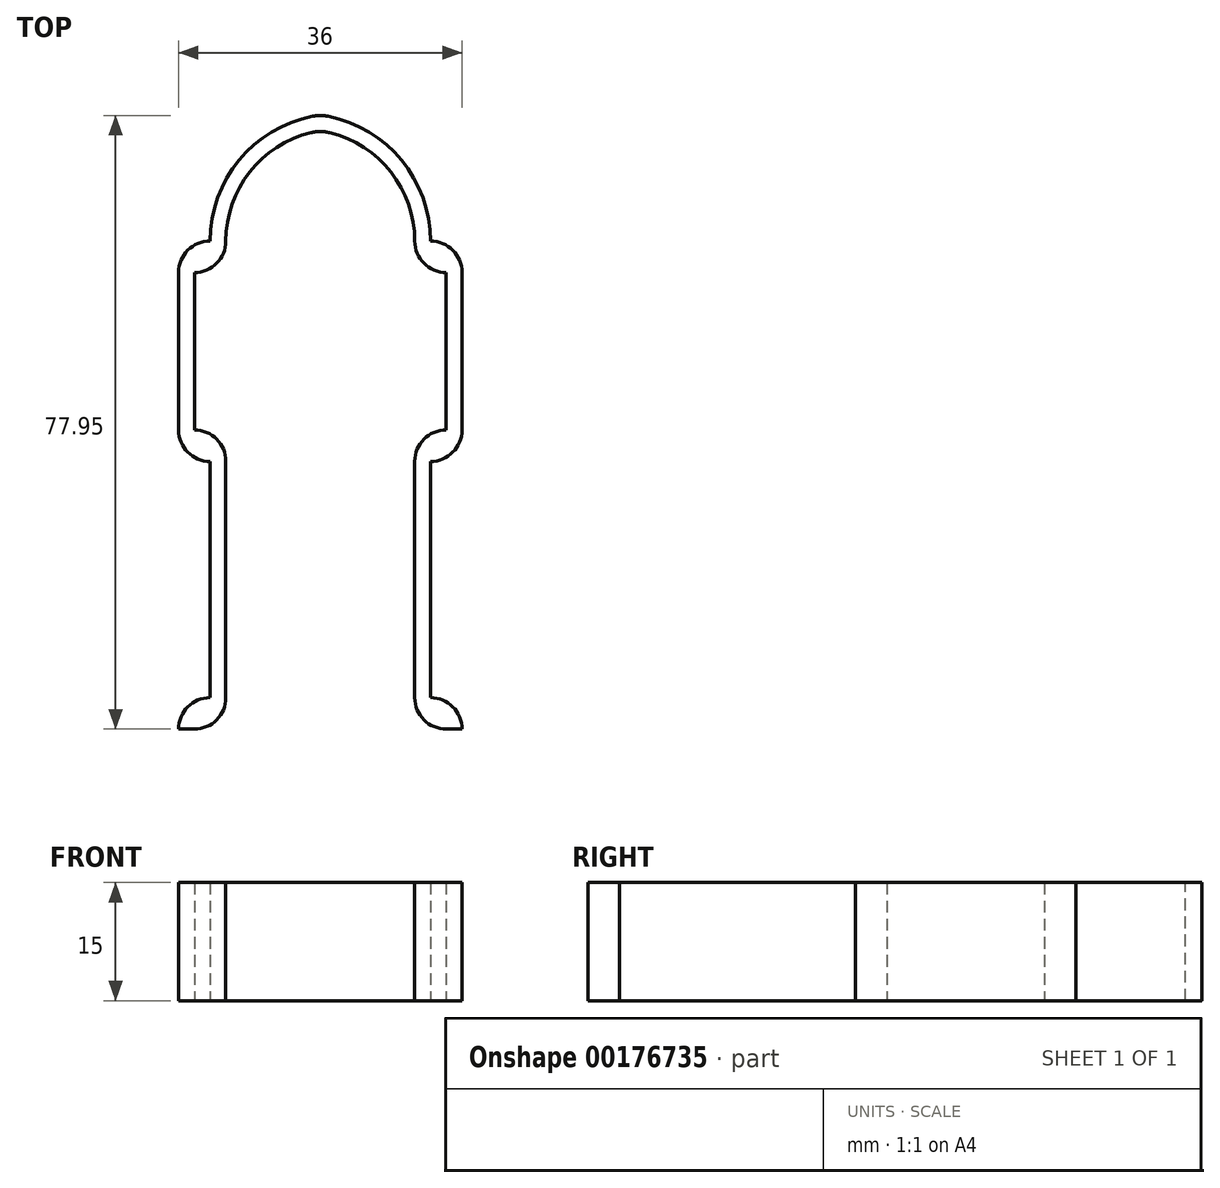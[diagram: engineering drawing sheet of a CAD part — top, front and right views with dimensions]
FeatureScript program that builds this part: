
annotation { "Feature Type Name" : "Feature", "Feature Type Description" : "" }
export const myFeature = defineFeature(function(context is Context, id is Id, definition is map)
    precondition{}
    {
        {
            var Q0;
            Q0=qCreatedBy(makeId("Top.planeOp"),FACE);
            var sketch = newSketch(context, id + "F0", { "sketchPlane" : qUnion([Q0])});
            skLineSegment(sketch, "E0", {"start": v(0, 33.75) * mm, "end": v(0, -40.7) * mm, "construction": true});
            skLineSegment(sketch, "E1.0", {"start": v(-16, 33.75) * mm, "end": v(-16, -40.7) * mm, "construction": true});
            skLineSegment(sketch, "E2", {"start": v(-23, 0) * mm, "end": v(0, 0) * mm, "construction": true});
            skLineSegment(sketch, "E3.0", {"start": v(-23, 14) * mm, "end": v(0, 14) * mm, "construction": true});
            skLineSegment(sketch, "E4.0", {"start": v(-23, 28) * mm, "end": v(0, 28) * mm, "construction": true});
            skLineSegment(sketch, "E5.MirrorCS", {"start": v(-23, -28) * mm, "end": v(0, -28) * mm, "construction": true});
            skLineSegment(sketch, "E6.MirrorCS", {"start": v(-23, -14) * mm, "end": v(0, -14) * mm, "construction": true});
            skArc(sketch, "E7", {"start": v(-16, 9.8) * mm, "mid": v(-11.8, 14) * mm, "end": v(-16, 18.2) * mm});
            skArc(sketch, "E8.MirrorC", {"start": v(-16, -9.8) * mm, "mid": v(-11.8, -14) * mm, "end": v(-16, -18.2) * mm});
            skLineSegment(sketch, "E9", {"start": v(0, 28) * mm, "end": v(-11, 28) * mm});
            skLineSegment(sketch, "E10", {"start": v(-16, 23) * mm, "end": v(-16, 18.2) * mm});
            skLineSegment(sketch, "E11", {"start": v(-16, 9.8) * mm, "end": v(-16, -9.8) * mm});
            skLineSegment(sketch, "E12", {"start": v(-16, -28) * mm, "end": v(-16, -47.92) * mm});
            skPoint(sketch, "E13.visualSharp", {"position": v(-16, 28) * mm});
            skArc(sketch, "E13.filletArc", {"start": v(-11, 28) * mm, "mid": v(-14.54, 26.54) * mm, "end": v(-16, 23) * mm});
            skLineSegment(sketch, "E14.0", {"start": v(-18, -11.7) * mm, "end": v(-18, -51.66) * mm});
            skLineSegment(sketch, "E15.0", {"start": v(-18, 8.3) * mm, "end": v(-18, -8.3) * mm});
            skLineSegment(sketch, "E16.0", {"start": v(0, 30) * mm, "end": v(-7.5, 30) * mm});
            skLineSegment(sketch, "E17.0", {"start": v(-18, 19.94) * mm, "end": v(-18, 11.7) * mm});
            skLineSegment(sketch, "E18", {"start": v(-18, -8.3) * mm, "end": v(-18, -11.7) * mm});
            skLineSegment(sketch, "E19", {"start": v(-18, 11.7) * mm, "end": v(-18, 8.3) * mm});
            skLineSegment(sketch, "E20.MirrorCS", {"start": v(0, 30) * mm, "end": v(7.5, 30) * mm});
            skLineSegment(sketch, "E21.MirrorCS", {"start": v(0, 28) * mm, "end": v(11, 28) * mm});
            skArc(sketch, "E22.MirrorCS", {"start": v(11, 28) * mm, "mid": v(14.54, 26.54) * mm, "end": v(16, 23) * mm});
            skLineSegment(sketch, "E23.MirrorCS", {"start": v(18, 8.3) * mm, "end": v(18, -8.3) * mm});
            skLineSegment(sketch, "E24.MirrorCS", {"start": v(16, -23.2) * mm, "end": v(16, -47.92) * mm});
            skLineSegment(sketch, "E25.MirrorCS", {"start": v(18, -11.7) * mm, "end": v(18, -51.66) * mm});
            skArc(sketch, "E26.MirrorCS", {"start": v(16, -9.8) * mm, "mid": v(11.8, -14) * mm, "end": v(16, -18.2) * mm});
            skArc(sketch, "E27.MirrorCS", {"start": v(16, 9.8) * mm, "mid": v(11.8, 14) * mm, "end": v(16, 18.2) * mm});
            skLineSegment(sketch, "E28.MirrorCS", {"start": v(16, 9.8) * mm, "end": v(16, -9.8) * mm});
            skLineSegment(sketch, "E29.MirrorCS", {"start": v(18, -8.3) * mm, "end": v(18, -11.7) * mm});
            skLineSegment(sketch, "E30.MirrorCS", {"start": v(18, 11.7) * mm, "end": v(18, 8.3) * mm});
            skLineSegment(sketch, "E31.MirrorCS", {"start": v(16, 23) * mm, "end": v(16, 18.2) * mm});
            skLineSegment(sketch, "E32.MirrorCS", {"start": v(18, 19.94) * mm, "end": v(18, 11.7) * mm});
            skLineSegment(sketch, "E33", {"start": v(-11.8, -14) * mm, "end": v(-11.8, -28) * mm});
            skLineSegment(sketch, "E34", {"start": v(-11.8, -28) * mm, "end": v(-16, -23.2) * mm});
            skLineSegment(sketch, "E35.MirrorCS", {"start": v(11.8, -14) * mm, "end": v(11.8, -28) * mm});
            skLineSegment(sketch, "E36.MirrorCS", {"start": v(11.8, -28) * mm, "end": v(16, -23.2) * mm});
            skPoint(sketch, "E37.orphan", {"position": v(16, -18.2) * mm});
            skLineSegment(sketch, "E38", {"start": v(-16, -47.92) * mm, "end": v(-18, -51.66) * mm});
            skLineSegment(sketch, "E39", {"start": v(-11.8, -28) * mm, "end": v(-16, -30.26) * mm});
            skLineSegment(sketch, "E40.MirrorCS", {"start": v(11.8, -28) * mm, "end": v(16, -30.26) * mm});
            skLineSegment(sketch, "E41.MirrorCS", {"start": v(16, -47.92) * mm, "end": v(18, -51.66) * mm});
            skLineSegment(sketch, "E42", {"start": v(0, 30) * mm, "end": v(-11, 30) * mm});
            skArc(sketch, "E43", {"start": v(-11, 30) * mm, "mid": v(-17.13, 26.8) * mm, "end": v(-18, 19.94) * mm});
            skLineSegment(sketch, "E44.MirrorCS", {"start": v(0, 30) * mm, "end": v(11, 30) * mm});
            skArc(sketch, "E45.MirrorCS", {"start": v(11, 30) * mm, "mid": v(17.13, 26.8) * mm, "end": v(18, 19.94) * mm});
            skSolve(sketch);
        }
        {
            var Q0;
            Q0=qCreatedBy(makeId("Top.planeOp"),FACE);
            var sketch = newSketch(context, id + "F1", { "sketchPlane" : qUnion([Q0])});
            skLineSegment(sketch, "E46.0", {"start": v(-23, 28) * mm, "end": v(0, 28) * mm, "construction": true});
            skLineSegment(sketch, "E47.0", {"start": v(0, 33.75) * mm, "end": v(0, -40.7) * mm, "construction": true});
            skLineSegment(sketch, "E48.0", {"start": v(-23, 0) * mm, "end": v(0, 0) * mm, "construction": true});
            skLineSegment(sketch, "E49.0", {"start": v(-16, 33.75) * mm, "end": v(-16, 14) * mm, "construction": true});
            skLineSegment(sketch, "E50.0", {"start": v(-12, 33.75) * mm, "end": v(-12, 14) * mm, "construction": true});
            skLineSegment(sketch, "E51.0", {"start": v(-23, 14) * mm, "end": v(0, 14) * mm, "construction": true});
            skLineSegment(sketch, "E52.0", {"start": v(-23, -14) * mm, "end": v(0, -14) * mm, "construction": true});
            skArc(sketch, "E53", {"start": v(-16, 10) * mm, "mid": v(-13.17, 11.17) * mm, "end": v(-12, 14) * mm});
            skArc(sketch, "E54.trimOffspring", {"start": v(-12, -14) * mm, "mid": v(-13.17, -11.17) * mm, "end": v(-16, -10) * mm});
            skLineSegment(sketch, "E55.trimOffspring", {"start": v(-12, -14) * mm, "end": v(-12, -40.7) * mm, "construction": true});
            skLineSegment(sketch, "E56.0", {"start": v(-14, 33.75) * mm, "end": v(-14, 14) * mm, "construction": true});
            skLineSegment(sketch, "E57.0", {"start": v(-14, -14) * mm, "end": v(-14, -40.7) * mm, "construction": true});
            skLineSegment(sketch, "E58.trimOffspring", {"start": v(-16, 10) * mm, "end": v(-16, -10) * mm, "construction": true});
            skLineSegment(sketch, "E59.trimOffspring", {"start": v(-16, -14) * mm, "end": v(-16, -40.7) * mm, "construction": true});
            skLineSegment(sketch, "E60.0", {"start": v(-18, 10) * mm, "end": v(-18, -10) * mm, "construction": true});
            skArc(sketch, "E61", {"start": v(-18, 10) * mm, "mid": v(-16.83, 12.83) * mm, "end": v(-14, 14) * mm});
            skArc(sketch, "E62", {"start": v(-18, -10) * mm, "mid": v(-16.83, -12.83) * mm, "end": v(-14, -14) * mm});
            skArc(sketch, "E63", {"start": v(-12, 14) * mm, "mid": v(-8.59, 23.22) * mm, "end": v(0, 28) * mm});
            skLineSegment(sketch, "E64.0", {"start": v(-23, 30) * mm, "end": v(0, 30) * mm, "construction": true});
            skArc(sketch, "E65.0", {"start": v(-14, 14) * mm, "mid": v(-10.1, 24.52) * mm, "end": v(-0.3, 29.98) * mm});
            skLineSegment(sketch, "E66.0", {"start": v(-23, -29) * mm, "end": v(0, -29) * mm, "construction": true});
            skArc(sketch, "E67.MirrorCS", {"start": v(-12, -44) * mm, "mid": v(-13.17, -46.83) * mm, "end": v(-16, -48) * mm});
            skArc(sketch, "E68.MirrorCS", {"start": v(-18, -48) * mm, "mid": v(-16.83, -45.17) * mm, "end": v(-14, -44) * mm});
            skLineSegment(sketch, "E69", {"start": v(-12, -14) * mm, "end": v(-12, -44) * mm});
            skLineSegment(sketch, "E70", {"start": v(-14, -44) * mm, "end": v(-14, -14) * mm});
            skLineSegment(sketch, "E71", {"start": v(-16, -48) * mm, "end": v(-18, -48) * mm});
            skLineSegment(sketch, "E72", {"start": v(-18, -10) * mm, "end": v(-18, 10) * mm});
            skLineSegment(sketch, "E73", {"start": v(-16, 10) * mm, "end": v(-16, -10) * mm});
            skLineSegment(sketch, "E74", {"start": v(0, 30) * mm, "end": v(0, 28) * mm});
            skLineSegment(sketch, "E75", {"start": v(-0.3, 29.98) * mm, "end": v(0, 30) * mm});
            skArc(sketch, "E76.MirrorCS", {"start": v(12, -14) * mm, "mid": v(13.17, -11.17) * mm, "end": v(16, -10) * mm});
            skArc(sketch, "E77.MirrorCS", {"start": v(18, -10) * mm, "mid": v(16.83, -12.83) * mm, "end": v(14, -14) * mm});
            skLineSegment(sketch, "E78.MirrorCS", {"start": v(16, 10) * mm, "end": v(16, -10) * mm, "construction": true});
            skLineSegment(sketch, "E79.MirrorCS", {"start": v(18, 10) * mm, "end": v(18, -10) * mm, "construction": true});
            skArc(sketch, "E80.MirrorCS", {"start": v(16, 10) * mm, "mid": v(13.17, 11.17) * mm, "end": v(12, 14) * mm});
            skArc(sketch, "E81.MirrorCS", {"start": v(18, 10) * mm, "mid": v(16.83, 12.83) * mm, "end": v(14, 14) * mm});
            skArc(sketch, "E82.MirrorCS", {"start": v(12, 14) * mm, "mid": v(8.59, 23.22) * mm, "end": v(0, 28) * mm});
            skArc(sketch, "E83.MirrorCS", {"start": v(14, 14) * mm, "mid": v(10.1, 24.52) * mm, "end": v(0.3, 29.98) * mm});
            skArc(sketch, "E84.MirrorCS", {"start": v(12, -44) * mm, "mid": v(13.17, -46.83) * mm, "end": v(16, -48) * mm});
            skLineSegment(sketch, "E85.MirrorCS", {"start": v(12, -14) * mm, "end": v(12, -44) * mm});
            skLineSegment(sketch, "E86.MirrorCS", {"start": v(14, -44) * mm, "end": v(14, -14) * mm});
            skArc(sketch, "E87.MirrorCS", {"start": v(18, -48) * mm, "mid": v(16.83, -45.17) * mm, "end": v(14, -44) * mm});
            skLineSegment(sketch, "E88.MirrorCS", {"start": v(16, -48) * mm, "end": v(18, -48) * mm});
            skLineSegment(sketch, "E89", {"start": v(18, 10) * mm, "end": v(18, -10) * mm});
            skLineSegment(sketch, "E90", {"start": v(16, -10) * mm, "end": v(16, 10) * mm});
            skLineSegment(sketch, "E91", {"start": v(0.3, 29.98) * mm, "end": v(0, 30) * mm});
            skSolve(sketch);
        }
        {
            var Q0;
            Q0=makeQuery(id+"F1.imprint","IMPRINT",FACE,{"disambiguationData":[TD([[makeQuery(id+"F1.imprint","IMPRINT",EDGE,{"derivedFrom":sQuery(id+"F1.wireOp",EDGE,"E74")}),1.0]])]});
            var Q1;
            Q1=makeQuery(id+"F1.imprint","IMPRINT",FACE,{"disambiguationData":[TD([[makeQuery(id+"F1.imprint","IMPRINT",EDGE,{"derivedFrom":sQuery(id+"F1.wireOp",EDGE,"E53")}),1.0]])]});
            extrude(context, id + "F2", {"entities" : qUnion([Q0, Q1]), "depth" : 15 * mm});
        }
        {
            var Q0;
            Q0=makeQuery(id+"F2.opExtrude","SWEPT_EDGE",EDGE,{"disambiguationData":[OSD([sQuery(id+"F1.wireOp",EDGE,"E74"),sQuery(id+"F1.wireOp",EDGE,"E75"),sQuery(id+"F1.wireOp",EDGE,"E91")])]});
            var Q1;
            Q1=makeQuery(id+"F2.opExtrude","SWEPT_EDGE",EDGE,{"disambiguationData":[OSD([sQuery(id+"F1.wireOp",EDGE,"E63"),sQuery(id+"F1.wireOp",EDGE,"E74"),sQuery(id+"F1.wireOp",EDGE,"E82.MirrorCS")])]});
            fillet(context, id + "F3", {"entities" : qUnion([Q0, Q1]), "radius" : 5 * mm, "tangentPropagation" : true, "allowEdgeOverflow" : false});
        }
    });
